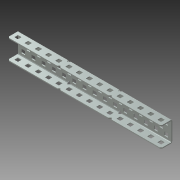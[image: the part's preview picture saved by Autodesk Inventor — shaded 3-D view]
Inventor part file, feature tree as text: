
AUTODESK INVENTOR PART (.ipt)
format: ipt  version: 2013 (Build 170138000, 138)  size: 1,650,176 bytes
history: native  units: mm (DEFAULTED — no unit token found)
features: other x74, extrude x74, pattern_linear x3, sketch x2, imported_body x1, plane x1, mirror x1
ambient origin geometry x8: Origin, YZ Plane, XZ Plane, XY Plane, X Axis, Y Axis, Z Axis, Center Point
bodies: Solid1 (feature_tree)
feature tree (156):
  imported_body  "Base1"
  sketch  "Sketch1"  dims[d1=1.1684mm]
  pattern_linear  "Rectangular Pattern1"  Spacing1=1.1684mm  [1 undecoded]
  pattern_linear  "Rectangular Pattern2"  Spacing1=0.0mm  [1 undecoded]
  pattern_linear  "Rectangular Pattern3"  Count1=15  [1 undecoded]
  plane  "Work Plane1"
  mirror  "Mirror1"
  other  "Srf1"
  other  "Srf2"
  other  "Srf3"
  other  "Srf4"
  other  "Srf5"
  other  "Srf6"
  other  "Srf17"
  other  "Srf18"
  other  "Srf19"
  other  "Srf20"
  other  "Srf21"
  other  "Srf32"
  other  "Srf33"
  other  "Srf34"
  other  "Srf7"
  other  "Srf8"
  other  "Srf9"
  other  "Srf10"
  other  "Srf11"
  other  "Srf12"
  other  "Srf13"
  other  "Srf14"
  other  "Srf15"
  other  "Srf16"
  other  "Srf22"
  other  "Srf23"
  other  "Srf24"
  other  "Srf25"
  other  "Srf26"
  other  "Srf27"
  other  "Srf28"
  other  "Srf29"
  other  "Srf30"
  other  "Srf31"
  other  "Srf35"
  other  "Srf36"
  other  "Srf37"
  other  "Srf38"
  other  "Srf39"
  other  "Srf40"
  other  "Srf41"
  other  "Srf42"
  other  "Srf43"
  other  "Srf44"
  sketch  "Sketch2"  dims[d2=0.0mm d3=1.1684mm d4=0.0mm d5=150.0mm d7=12.7mm d8=20.0mm d10=12.7mm d11=140.0mm d13=12.7mm d14=1.1684mm d15=0.0mm d16=150.0mm d18=12.7mm d19=0.0mm d20=0.0mm d21=0.0mm d22=0.0mm d23=0.0mm d24=0.0mm d25=0.0mm d26=0.0mm d27=0.0mm d28=0.0mm d29=0.0mm d30=0.0mm d31=0.0mm d32=0.0mm d33=0.0mm d34=0.0mm d35=0.0mm d36=0.0mm d37=0.0mm d38=0.0mm d39=0.0mm d40=0.0mm d41=0.0mm d42=0.0mm d43=0.0mm d44=0.0mm d45=0.0mm d46=0.0mm d47=0.0mm d48=0.0mm d49=0.0mm d50=0.0mm d51=0.0mm d52=0.0mm d53=0.0mm d54=0.0mm d55=0.0mm d56=0.0mm d57=0.0mm d58=0.0mm d59=0.0mm d60=0.0mm d61=0.0mm d62=0.0mm d63=0.0mm d64=0.0mm d65=0.0mm d66=0.0mm d67=0.0mm d68=0.0mm d69=0.0mm d70=0.0mm d71=0.0mm d72=0.0mm d73=0.0mm d74=0.0mm d75=0.0mm d76=0.0mm d77=0.0mm d78=0.0mm d79=0.0mm d80=0.0mm d81=0.0mm d82=0.0mm d83=0.0mm d84=0.0mm d85=0.0mm d86=0.0mm d87=0.0mm d88=0.0mm d89=0.0mm d90=0.0mm d91=0.0mm d92=0.0mm d93=0.0mm d94=0.0mm d95=0.0mm d96=0.0mm d97=0.0mm d98=0.0mm d99=0.0mm d100=0.0mm d101=0.0mm d102=0.0mm d103=0.0mm d104=0.0mm d105=0.0mm d106=0.0mm d107=0.0mm d108=0.0mm d109=0.0mm d110=0.0mm d111=0.0mm d112=0.0mm d113=0.0mm d114=0.0mm d115=0.0mm d116=0.0mm d117=0.0mm d118=0.0mm d119=0.0mm d120=0.0mm d121=0.0mm d122=0.0mm d123=0.0mm d124=0.0mm d125=0.0mm d126=0.0mm d127=0.0mm d128=0.0mm d129=0.0mm d130=0.0mm d131=0.0mm d132=0.0mm d133=0.0mm d134=0.0mm d135=0.0mm d136=0.0mm d137=0.0mm d138=0.0mm d139=0.0mm d140=0.0mm d141=0.0mm d142=0.0mm d143=0.0mm d144=0.0mm d145=0.0mm d146=0.0mm d147=0.0mm d148=0.0mm d149=0.0mm d150=0.0mm d151=0.0mm d152=0.0mm d153=0.0mm d154=0.0mm d155=0.0mm d156=0.0mm d157=0.0mm d158=0.0mm d159=0.0mm d160=0.0mm d161=0.0mm d162=0.0mm d163=0.0mm d164=0.0mm d165=0.0mm d166=0.0mm]
  other  "Srf45"
  other  "Srf46"
  other  "Srf47"
  other  "Srf48"
  other  "Srf49"
  other  "Srf50"
  other  "Srf51"
  other  "Srf52"
  other  "Srf53"
  other  "Srf54"
  other  "Srf55"
  other  "Srf56"
  other  "Srf57"
  other  "Srf58"
  other  "Srf59"
  other  "Srf60"
  other  "Srf61"
  other  "Srf62"
  other  "Srf63"
  other  "Srf64"
  other  "Srf65"
  other  "Srf66"
  other  "Srf67"
  other  "Srf68"
  other  "Srf69"
  other  "Srf70"
  other  "Srf71"
  other  "Srf72"
  other  "Srf73"
  other  "Srf74"
  extrude  "ExtrusionSrf1"  Depth=12.7mm
  extrude  "ExtrusionSrf2"  Depth=20.0mm
  extrude  "ExtrusionSrf45"  Depth=140.0mm
  extrude  "ExtrusionSrf3"  Depth=12.7mm
  extrude  "ExtrusionSrf4"  Depth=1.1684mm
  extrude  "ExtrusionSrf5"  TaperAngle=0.0deg  [1 undecoded]
  extrude  "ExtrusionSrf6"  Depth=150.0mm
  extrude  "ExtrusionSrf7"  Depth=12.7mm
  extrude  "ExtrusionSrf8"  TaperAngle=0.0deg  [1 undecoded]
  extrude  "ExtrusionSrf9"  TaperAngle=0.0deg  [1 undecoded]
  extrude  "ExtrusionSrf10"  TaperAngle=0.0deg  [1 undecoded]
  extrude  "ExtrusionSrf11"  TaperAngle=0.0deg  [1 undecoded]
  extrude  "ExtrusionSrf12"  TaperAngle=0.0deg  [1 undecoded]
  extrude  "ExtrusionSrf13"  TaperAngle=0.0deg  [1 undecoded]
  extrude  "ExtrusionSrf14"  TaperAngle=0.0deg  [1 undecoded]
  extrude  "ExtrusionSrf15"  TaperAngle=0.0deg  [1 undecoded]
  extrude  "ExtrusionSrf16"  TaperAngle=0.0deg  [1 undecoded]
  extrude  "ExtrusionSrf17"  TaperAngle=0.0deg  [1 undecoded]
  extrude  "ExtrusionSrf18"  TaperAngle=0.0deg  [1 undecoded]
  extrude  "ExtrusionSrf19"  TaperAngle=0.0deg  [1 undecoded]
  extrude  "ExtrusionSrf20"  TaperAngle=0.0deg  [1 undecoded]
  extrude  "ExtrusionSrf21"  TaperAngle=0.0deg  [1 undecoded]
  extrude  "ExtrusionSrf22"  TaperAngle=0.0deg  [1 undecoded]
  extrude  "ExtrusionSrf23"  TaperAngle=0.0deg  [1 undecoded]
  extrude  "ExtrusionSrf24"  TaperAngle=0.0deg  [1 undecoded]
  extrude  "ExtrusionSrf25"  TaperAngle=0.0deg  [1 undecoded]
  extrude  "ExtrusionSrf26"  TaperAngle=0.0deg  [1 undecoded]
  extrude  "ExtrusionSrf27"  TaperAngle=0.0deg  [1 undecoded]
  extrude  "ExtrusionSrf28"  TaperAngle=0.0deg  [1 undecoded]
  extrude  "ExtrusionSrf29"  TaperAngle=0.0deg  [1 undecoded]
  extrude  "ExtrusionSrf30"  TaperAngle=0.0deg  [1 undecoded]
  extrude  "ExtrusionSrf31"  TaperAngle=0.0deg  [1 undecoded]
  extrude  "ExtrusionSrf32"  TaperAngle=0.0deg  [1 undecoded]
  extrude  "ExtrusionSrf33"  TaperAngle=0.0deg  [1 undecoded]
  extrude  "ExtrusionSrf34"  TaperAngle=0.0deg  [1 undecoded]
  extrude  "ExtrusionSrf35"  TaperAngle=0.0deg  [1 undecoded]
  extrude  "ExtrusionSrf36"  TaperAngle=0.0deg  [1 undecoded]
  extrude  "ExtrusionSrf37"  TaperAngle=0.0deg  [1 undecoded]
  extrude  "ExtrusionSrf38"  TaperAngle=0.0deg  [1 undecoded]
  extrude  "ExtrusionSrf39"  TaperAngle=0.0deg  [1 undecoded]
  extrude  "ExtrusionSrf40"  TaperAngle=0.0deg  [1 undecoded]
  extrude  "ExtrusionSrf41"  TaperAngle=0.0deg  [1 undecoded]
  extrude  "ExtrusionSrf42"  TaperAngle=0.0deg  [1 undecoded]
  extrude  "ExtrusionSrf43"  TaperAngle=0.0deg  [1 undecoded]
  extrude  "ExtrusionSrf44"  TaperAngle=0.0deg  [1 undecoded]
  extrude  "ExtrusionSrf46"  TaperAngle=0.0deg  [1 undecoded]
  extrude  "ExtrusionSrf47"  TaperAngle=0.0deg  [1 undecoded]
  extrude  "ExtrusionSrf48"  TaperAngle=0.0deg  [1 undecoded]
  extrude  "ExtrusionSrf49"  TaperAngle=0.0deg  [1 undecoded]
  extrude  "ExtrusionSrf50"  TaperAngle=0.0deg  [1 undecoded]
  extrude  "ExtrusionSrf51"  TaperAngle=0.0deg  [1 undecoded]
  extrude  "ExtrusionSrf52"  TaperAngle=0.0deg  [1 undecoded]
  extrude  "ExtrusionSrf53"  TaperAngle=0.0deg  [1 undecoded]
  extrude  "ExtrusionSrf54"  TaperAngle=0.0deg  [1 undecoded]
  extrude  "ExtrusionSrf55"  TaperAngle=0.0deg  [1 undecoded]
  extrude  "ExtrusionSrf56"  TaperAngle=0.0deg  [1 undecoded]
  extrude  "ExtrusionSrf57"  TaperAngle=0.0deg  [1 undecoded]
  extrude  "ExtrusionSrf58"  TaperAngle=0.0deg  [1 undecoded]
  extrude  "ExtrusionSrf59"  TaperAngle=0.0deg  [1 undecoded]
  extrude  "ExtrusionSrf60"  TaperAngle=0.0deg  [1 undecoded]
  extrude  "ExtrusionSrf61"  TaperAngle=0.0deg  [1 undecoded]
  extrude  "ExtrusionSrf62"  TaperAngle=0.0deg  [1 undecoded]
  extrude  "ExtrusionSrf63"  TaperAngle=0.0deg  [1 undecoded]
  extrude  "ExtrusionSrf64"  TaperAngle=0.0deg  [1 undecoded]
  extrude  "ExtrusionSrf65"  TaperAngle=0.0deg  [1 undecoded]
  extrude  "ExtrusionSrf66"  TaperAngle=0.0deg  [1 undecoded]
  extrude  "ExtrusionSrf67"  TaperAngle=0.0deg  [1 undecoded]
  extrude  "ExtrusionSrf68"  TaperAngle=0.0deg  [1 undecoded]
  extrude  "ExtrusionSrf69"  TaperAngle=0.0deg  [1 undecoded]
  extrude  "ExtrusionSrf70"  TaperAngle=0.0deg  [1 undecoded]
  extrude  "ExtrusionSrf71"  TaperAngle=0.0deg  [1 undecoded]
  extrude  "ExtrusionSrf72"  TaperAngle=0.0deg  [1 undecoded]
  extrude  "ExtrusionSrf73"  TaperAngle=0.0deg  [1 undecoded]
  extrude  "ExtrusionSrf74"  TaperAngle=0.0deg  [1 undecoded]
note: 70 required parameter values undecoded (feature->parameter linkage not recoverable at this tier; creation-order binding heuristic only, values carry confidence <= 0.55)
